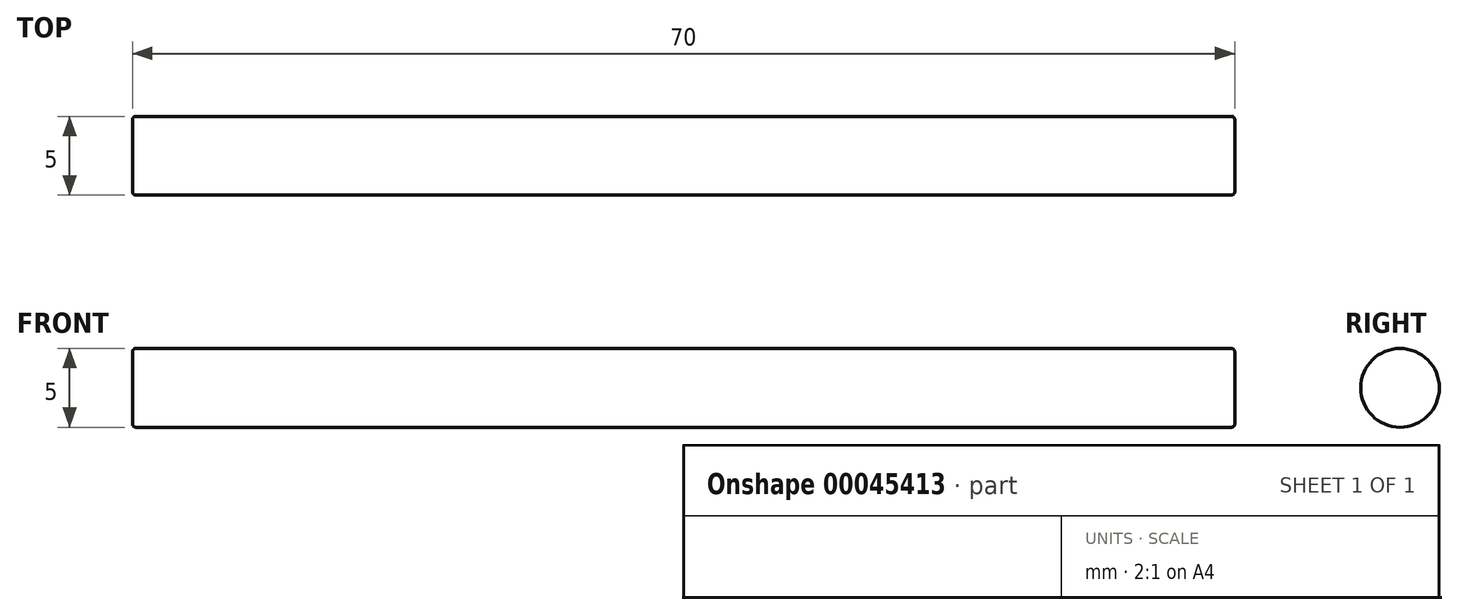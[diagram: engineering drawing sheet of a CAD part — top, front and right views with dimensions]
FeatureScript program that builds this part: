
annotation { "Feature Type Name" : "Feature", "Feature Type Description" : "" }
export const myFeature = defineFeature(function(context is Context, id is Id, definition is map)
    precondition{}
    {
        {
            var Q0;
            Q0=qCreatedBy(makeId("Right.planeOp"),FACE);
            var sketch = newSketch(context, id + "F0", { "sketchPlane" : qUnion([Q0])});
            skCircle(sketch, "E0", {"center": v(0, 0) * mm, "radius": 2.5 * mm});
            skSolve(sketch);
        }
        {
            var Q0;
            Q0=qSketchRegion(id+"F0",true);
            extrude(context, id + "F1", {"entities" : qUnion([Q0]), "endBound" : BoundingType.SYMMETRIC, "depth" : 70 * mm});
        }
        {
            var Q0;
            Q0=makeQuery(id+"F1.opExtrude","CAP_EDGE",EDGE,{"disambiguationData":[OSD([sQuery(id+"F0.wireOp",EDGE,"E0")])],"isStart":false});
            var Q1;
            Q1=makeQuery(id+"F1.opExtrude","CAP_EDGE",EDGE,{"disambiguationData":[OSD([sQuery(id+"F0.wireOp",EDGE,"E0")])],"isStart":true});
            fillet(context, id + "F2", {"entities" : qUnion([Q0, Q1]), "radius" : 0.2 * mm, "tangentPropagation" : true, "allowEdgeOverflow" : false});
        }
    });
